# Revit family: Electronics_Commercial-Audio_Biamp_Stereo-Preamplifier_PREZONE-1
name_source: partatom
category: Communication Devices
units: mm (PartAtom-declared; Revit-internal decimal feet)

## family parameters
Cut with Voids When Loaded = No
Host = Face
Maintain Annotation Orientation = No
OmniClass Number = 23.85.10.11.14
OmniClass Title = Audio Equipment
Part Type = Normal
Room Calculation Point = No
Round Connector Dimension = Use Diameter
Shared = No

## types (1)
- PREZONE1
    Apparent Load = 30 VA
    Connector Description = 240V DC 30W
    Default Elevation = 4' - 0"
    Depth = 0' - 11 13/32"
    Description = PREZONE1 Stereo Pre-Amplifier/Mixer with 2 Stereo Volume Zones
    Emergency input = Yes
    Frequency response (in Hz) = 20-25 k
    Height = 0' - 3 1/2"
    Housing Material = Biamp - Metal - Black
    Line input unbalanced = 4
    MIC inputs balanced = 2
    MIC level control = Yes
    Manufacturer = Biamp
    Max Power Consumption = 30 W
    Model = PREZONE1
    Music level control = Yes
    Number of Poles = 1
    Power Factor = 1
    Prioriti levels = 3
    Product Documentation Link = https://downloads.biamp.com
    Product Page URL = https://www.biamp.com
    Product data url = https://www.bimobject.com
    Tone control = Yes
    URL = https://www.biamp.com
    VOX mute = Yes
    Voltage = 120 V
    Weight = 8.05 lbf
    Width = 1' - 4 15/16"

## geometry (parser evidence)
native form markers: Sweep x2
no freeform markers — native parametric forms only
